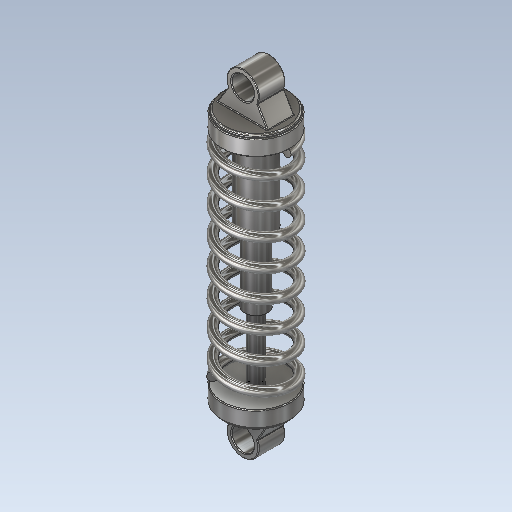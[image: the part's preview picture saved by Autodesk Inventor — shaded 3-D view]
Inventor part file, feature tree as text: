
AUTODESK INVENTOR PART (.ipt)
format: ipt  version: 2020 (Build 240168000, 168)  size: 848,384 bytes
history: native  units: in
note: dims shown in document units (in); Inventor stores cm internally (conversion verified against a paired STEP export)
features: fillet x26, sketch x17, revolve x5, extrude x4, plane x4, mirror x1, sweep x1, other x1
ambient origin geometry x8: Origin, YZ Plane, XZ Plane, XY Plane, X Axis, Y Axis, Z Axis, Center Point
bodies: Solid1 (feature_tree)
feature tree (59):
  revolve  "Revolution1"  [1 undecoded]
  sketch  "Sketch2"  dims[d3=1.0in d4=0.0in d7=1.0in d8=0.0in]
  extrude  "Extrusion1"  Depth=1.0in TaperAngle=0.0deg
  extrude  "Extrusion2"  Depth=0.05in
  extrude  "Extrusion3"  TaperAngle=90.0deg  [1 undecoded]
  extrude  "Extrusion4"  TaperAngle=90.0deg  [1 undecoded]
  fillet  "Fillet1"  [1 undecoded]
  fillet  "Fillet2"  Radius=4.0975in
  revolve  "Revolution2"  [1 undecoded]
  revolve  "Revolution3"  [1 undecoded]
  revolve  "Revolution4"  [1 undecoded]
  revolve  "Revolution5"  [1 undecoded]
  sketch  "Sketch11"
  plane  "Work Plane1"
  mirror  "Mirror1"
  plane  "Work Plane3"
  sketch  "Sketch14"
  sketch  "Sketch18"
  plane  "Work Plane7"
  sketch  "Sketch19"
  sketch  "3D Sketch3"
  plane  "Work Plane8"
  sketch  "Sketch20"
  sweep  "Sweep3"
  fillet  "Fillet3"  Radius=0.03in
  fillet  "Fillet4"  Radius=0.03in
  fillet  "Fillet5"  Radius=0.03in
  fillet  "Fillet6"  Radius=0.03in
  fillet  "Fillet7"  Radius=0.03in
  fillet  "Fillet8"  Radius=0.03in
  fillet  "Fillet9"  Radius=0.03in
  fillet  "Fillet10"  Radius=0.03in
  fillet  "Fillet11"  Radius=0.03in
  fillet  "Fillet12"  Radius=0.03in
  fillet  "Fillet13"  Radius=0.03in
  fillet  "Fillet14"  Radius=0.03in
  fillet  "Fillet15"  Radius=0.03in
  fillet  "Fillet16"  Radius=0.03in
  fillet  "Fillet17"  Radius=0.03in
  fillet  "Fillet18"  Radius=0.03in
  fillet  "Fillet19"  Radius=0.03in
  fillet  "Fillet20"  Radius=0.03in
  fillet  "Fillet21"  [1 undecoded]
  fillet  "Fillet22"  [1 undecoded]
  fillet  "Fillet23"  [1 undecoded]
  fillet  "Fillet24"  [1 undecoded]
  fillet  "Fillet25"  [1 undecoded]
  fillet  "Fillet26"  [1 undecoded]
  sketch  "Sketch1"  dims[d0=90.0deg d1=0.1in d2=0.0in]
  sketch  "Sketch3"  dims[d9=1.0in d10=0.0in d11=0.05in]
  sketch  "Sketch4"  dims[d12=0.03in d13=90.0deg]
  sketch  "Sketch5"  dims[d14=90.0deg d15=90.0deg d16=90.0deg d17=4.0975in]
  sketch  "Sketch6"  dims[d29=-0.163in d42=0.163in]
  sketch  "Sketch7"  dims[d43=1.0in d44=7.869in d45=2.3in d46=0.0in d47=90.0deg d48=90.0deg d49=90.0deg d50=90.0deg d51=0.0in d52=0.0in]
  sketch  "Sketch8"  dims[d53=0.03in d54=0.03in]
  sketch  "Sketch9"  dims[d55=0.03in d56=0.03in]
  sketch  "Sketch10"  dims[d57=0.02in d58=0.03in d59=0.03in d60=0.03in d61=0.03in d62=0.03in d63=0.03in d64=0.03in d65=0.03in d66=0.03in d67=0.03in d68=0.03in d69=0.03in d70=0.03in d71=0.03in d72=0.03in d73=0.03in d74=0.03in d75=0.03in d76=0.03in]
  other  "Helical Curve3"
  sketch  "Sketch21"
note: 14 required parameter values undecoded (feature->parameter linkage not recoverable at this tier; creation-order binding heuristic only, values carry confidence <= 0.55)